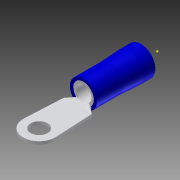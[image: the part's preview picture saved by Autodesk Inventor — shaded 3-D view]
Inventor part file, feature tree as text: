
AUTODESK INVENTOR PART (.ipt)
format: ipt  version: 2011 (Build 150239000, 239)  size: 133,632 bytes
history: native  units: mm
features: other x4, plane x2, imported_body x1, sketch x1
ambient origin geometry x8: Origin, YZ Plane, XZ Plane, XY Plane, X Axis, Y Axis, Z Axis, Center Point
bodies: Solid1 (feature_tree)
feature tree (8):
  imported_body  "Base1"
  sketch  "Sketch1"  dims[d0=3.175mm d1=6.35mm]
  other  "Work Point2"
  other  "Work Point3"
  plane  "Work Plane1"
  other  "Work Axis1"
  plane  "Work Plane2"
  other  "Work Axis2"
